# Revit family: Gira_2046112
name_source: partatom
category: Elektroinstallationen
revit_build: Autodesk Revit 2017 (Build: 20160225_1515(x64)
units: mm (PartAtom-declared; Revit-internal decimal feet)

## family parameters
Basisbauteil = Fläche
Beim Laden mit Abzugskörper schneiden = Nein
Bemaßung runder Anschluss = Durchmesser verwenden
Beschriftungsausrichtung beibehalten = Nein
Gemeinsam genutzt = Nein
Raumberechnungspunkt = Nein
Teiletyp = Normal

## types (1)
- KNX Tastsens.3 Plus 6f (2+4) Flächenschalter Reinweiß
    Andere Bussysteme = ohne
    Anzahl der Betätigungspunkte = 14
    Anzahl der Tasten = 6
    Ausführung der Oberfläche = glänzend
    BIM = https://media.stage.bim.site Tastsensor 3 Plus 6fach (2+4).rfa
    BIMSITE_PRODUCT_ID = 25e1e1edba6d511075fcef10d293e2c837b953b3
    Beschreibung = KNX Tastsensor 3 Plus 6fach (2+4)  Reinweiß glänzend Merkmale:  Montage auf Busankoppler 3 oder Busankoppler 3 externer Fühler.  Demontageschutz durch Verschraubung.  Grafikdisplay mit Hintergrundbeleuchtung und vielfältigen Anzeigemöglichkeiten, z. B. Temperatur, Uhrzeit, Datum, Alarm- und Hinweistexte.  Weiße Betriebs-LED.  Mehrfarbige Status-LED (rot, grün, blau) über die ETS parametrierbar.  Interner Temperatursensor zum Messen der lokalen Raumtemperatur. Tastsensor-Eigenschaften::  Wippen- oder Tastenfunktion für jede Bedienfläche einstellbar.  Wippenfunktion: Schalten, Dimmen, Jalousiesteuerung, Wertgeber 1 Byte, Wertgeber 2 Byte, Szenennebenstelle, 2-Kanal-Bedienung und manuelle Lüftersteuerung.  Tastenfunktion: Schalten, Dimmen, Jalousiesteuerung, Wertgeber 1 Byte, Wertgeber 2 Byte, Szenennebenstelle, 2-Kanal-Bedienung, Reglernebenstelle, Reglerbedienung, Heizungsuhrbedienung und manuelle Lüftersteuerung.  Reglernebenstelle oder Reglerbedienung: Betriebsmodusumschaltung, (definierte Wahl eines Betriebsmodus oder Wechsel zwischen verschiedenen Betriebsmodi bei Reglernebenstelle), Wechsel des Präsenzzustands, Sollwertverschiebung.  Sperrobjekt zum Sperren von einzelnen Tasten- bzw. Wippenfunktionen.  Anzeige einer Alarmmeldung durch Blinken sämtlicher LEDs.  Mehrfarbige Status-LED (rot, grün, blau) ist global oder jeweils getrennt konfigurierbar. Über den Bus kann eine überlagerte Funktion aktiviert werden, wodurch Farbe und Anzeigeinformation einzelner Status-LEDs prioritätsbedingt verändert werden können.  Betriebs-LED EIN, AUS, automatische Abschaltung oder über Objekt schaltbar.  Kommunikationsobjekt zur Helligkeitssteuerung der Status-LED, Beschriftungsfeldbeleuchtung und Hintergrundbeleuchtung des Displays. Raumtemperaturregler-Eigenschaften::  Betriebsmodi: Komfort, Stand-by, Nacht und Frost- bzw. Hitzeschutz mit jeweils eigenen Temperatursollwerten (für Heizen und bzw. oder Kühlen).  Komfortverlängerung durch Präsenztaste.  Frost- bzw. Hitzeschutzumschaltung durch Fensterstatus oder durch Frostschutzautomatik.  Anzeige der Raumtemperaturregler-Informationen über das Gerätedisplay.  Wahlweise ein oder zwei Regelkreise.  Je Heiz- oder Kühlstufe sind verschiedene Regelungsarten konfigurierbar: PI-Regelung (stetige oder schaltende PWM) oder 2-Punkt-Regelung (schaltend).  Regelparameter für PI-Regler und 2-Punkt-Regler einstellbar.  Interner Temperatursensor und bis zu zwei externe Temperaturfühler (1 x Objekt, 1 x bedrahtet) zur Raumtemperaturmessung möglich.  Optionaler externer bedrahteter Fernfühler für z. B. Estrichfühler bei Fußbodenheizung.  Heizungsuhr mit 28 Schaltzeiten. LC-Display Eigenschaften::  Grafikdisplay mit schaltbarer LED-Hintergrundbeleuchtung.  1-Bereichs- oder 2-Bereichsdarstellung.  Textanzeigen im Display in den Sprachen: Deutsch, Englisch, Niederländisch, Norwegisch, Russisch und Polnisch. Weitere Sprachen im Internet verfügbar.  Hinweise :  Professionelle Beschriftung über den Gira Beschriftungsservice www.beschriftung.gira.de.
    Bussystem Funkbus = Nein
    Bussystem KNX = Ja
    Bussystem KNX-Funk = Nein
    Bussystem LON = Nein
    Bussystem Powernet = Nein
    Datenblatt = https://media.stage.bim.site
    Datenblatt 1 = https://media.stage.bim.site
    Farbe = weiß
    GTIN = 4010337081968
    HAN = 2046112
    HeinzeBIM = https://www.heinze.de
    Hersteller = Gira
    Kosten = 0 $
    Mit Beschriftungsfeld = Nein
    Mit Busankopplung = Nein
    Mit Diebstahl-/Demontageschutz = Ja
    Mit Display = Ja
    Mit Infrarotsensor = Nein
    Mit LED-Anzeige = Ja
    Mit Raumthermostat = Ja
    Montageart = Unterputz
    Oberfläche Text = sonstige
    Produktseite = https://media.stage.bim.site
    RAL-Nummer (ähnlich) = 9010
    Schutzart (IP) = IP20
    Transparent = Nein
    Typname = KNX Tastsens.3 Plus 6f (2+4) Flächenschalter Reinweiß
    URL = https://www.gira.de
    Vorgabe-Ansicht = 1219 mm
    Werkstoff Text = Kunststoff
    Werkstoffgüte = Thermoplast

## geometry (parser evidence)
native form markers: Sweep x2
no freeform markers — native parametric forms only
